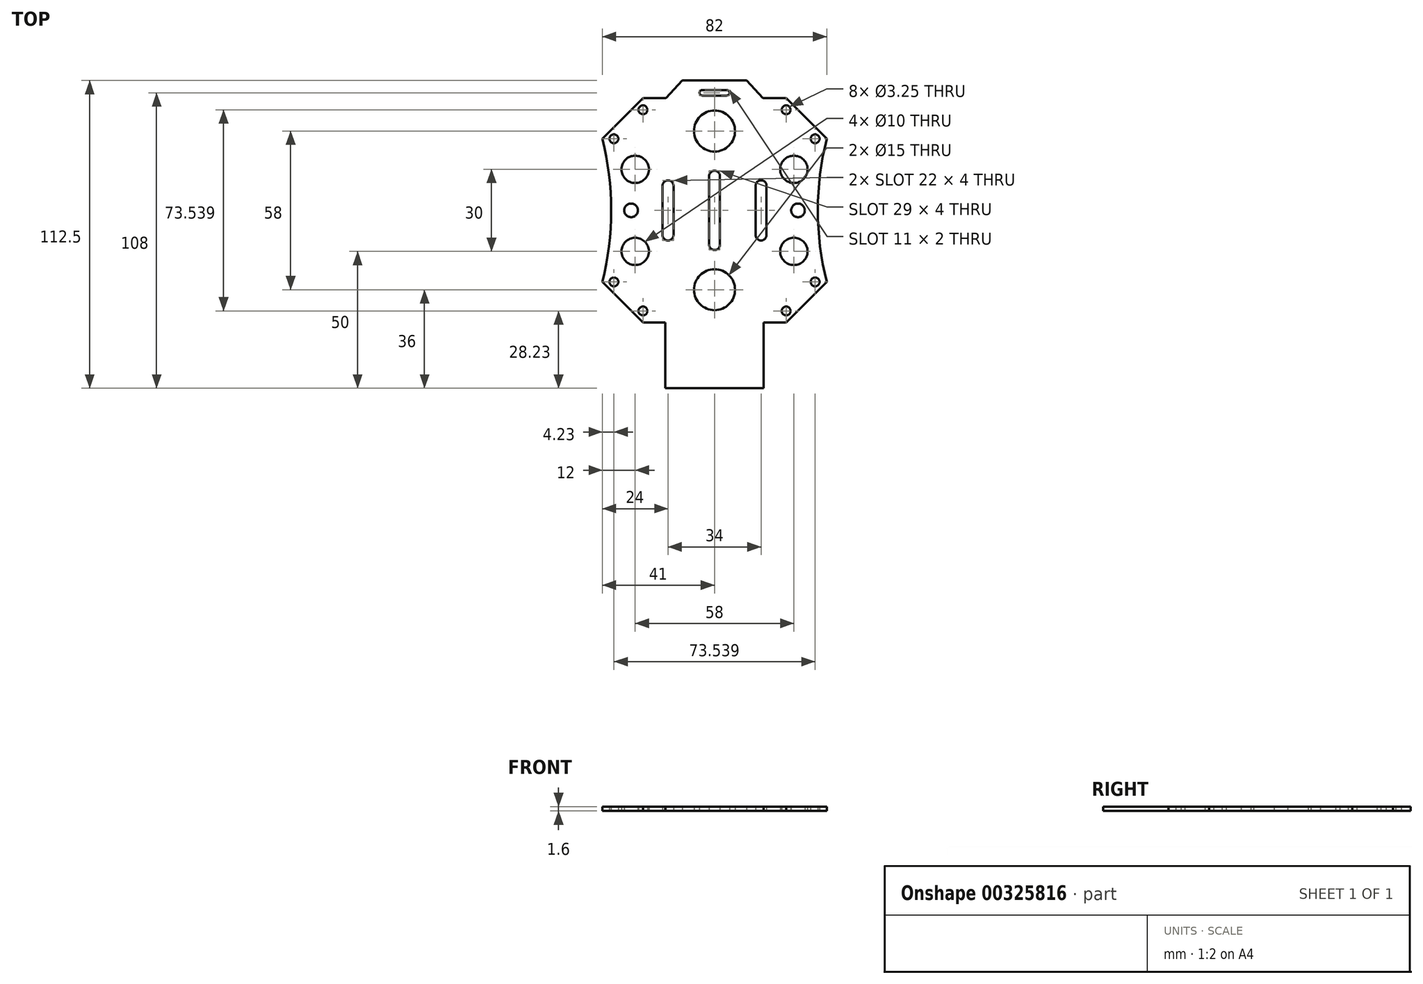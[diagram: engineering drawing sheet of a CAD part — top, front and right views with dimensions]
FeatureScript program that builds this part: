
annotation { "Feature Type Name" : "Feature", "Feature Type Description" : "" }
export const myFeature = defineFeature(function(context is Context, id is Id, definition is map)
    precondition{}
    {
        {
            var Q0;
            Q0=qCreatedBy(makeId("Top.planeOp"),FACE);
            var sketch = newSketch(context, id + "F0", { "sketchPlane" : qUnion([Q0])});
            skLineSegment(sketch, "E0.left", {"start": v(-2, 12.5) * mm, "end": v(-2, -12.5) * mm});
            skLineSegment(sketch, "E0.right", {"start": v(2, 12.5) * mm, "end": v(2, -12.5) * mm});
            skLineSegment(sketch, "E1", {"start": v(0, 0) * mm, "end": v(0, 54.3) * mm, "construction": true});
            skArc(sketch, "E2", {"start": v(2, 12.5) * mm, "mid": v(0, 14.5) * mm, "end": v(-2, 12.5) * mm});
            skArc(sketch, "E3", {"start": v(-2, -12.5) * mm, "mid": v(0, -14.5) * mm, "end": v(2, -12.5) * mm});
            skLineSegment(sketch, "E4", {"start": v(-64.66, 0) * mm, "end": v(96.62, 0) * mm, "construction": true});
            skLineSegment(sketch, "E5.left", {"start": v(-19, 9) * mm, "end": v(-19, -9) * mm});
            skLineSegment(sketch, "E5.right", {"start": v(-15, 9) * mm, "end": v(-15, -9) * mm});
            skArc(sketch, "E6", {"start": v(-15, 9) * mm, "mid": v(-17, 11) * mm, "end": v(-19, 9) * mm});
            skArc(sketch, "E7", {"start": v(-19, -9) * mm, "mid": v(-17, -11) * mm, "end": v(-15, -9) * mm});
            skArc(sketch, "E8.MirrorCS", {"start": v(19, -9) * mm, "mid": v(17, -11) * mm, "end": v(15, -9) * mm});
            skArc(sketch, "E9.MirrorCS", {"start": v(15, 9) * mm, "mid": v(17, 11) * mm, "end": v(19, 9) * mm});
            skLineSegment(sketch, "E10.MirrorCS", {"start": v(15, 9) * mm, "end": v(15, -9) * mm});
            skLineSegment(sketch, "E11.MirrorCS", {"start": v(19, 9) * mm, "end": v(19, -9) * mm});
            skCircle(sketch, "E12", {"center": v(-30.5, 0) * mm, "radius": 2.5 * mm});
            skCircle(sketch, "E13.MirrorC", {"center": v(30.5, 0) * mm, "radius": 2.5 * mm});
            skCircle(sketch, "E14", {"center": v(0, 29) * mm, "radius": 7.5 * mm});
            skCircle(sketch, "E15.MirrorC", {"center": v(0, -29) * mm, "radius": 7.5 * mm});
            skCircle(sketch, "E16", {"center": v(-29, 15) * mm, "radius": 5 * mm});
            skCircle(sketch, "E17.MirrorC", {"center": v(29, 15) * mm, "radius": 5 * mm});
            skCircle(sketch, "E18.MirrorC", {"center": v(-29, -15) * mm, "radius": 5 * mm});
            skCircle(sketch, "E19.MirrorC", {"center": v(29, -15) * mm, "radius": 5 * mm});
            skLineSegment(sketch, "E20.bottom", {"start": v(-4.5, 44) * mm, "end": v(4.5, 44) * mm});
            skLineSegment(sketch, "E20.top", {"start": v(-4.5, 42) * mm, "end": v(4.5, 42) * mm});
            skLineSegment(sketch, "E20.left", {"start": v(-4.5, 44) * mm, "end": v(-4.5, 42) * mm, "construction": true});
            skLineSegment(sketch, "E20.right", {"start": v(4.5, 44) * mm, "end": v(4.5, 42) * mm, "construction": true});
            skArc(sketch, "E21", {"start": v(-4.5, 44) * mm, "mid": v(-5.5, 43) * mm, "end": v(-4.5, 42) * mm});
            skArc(sketch, "E22", {"start": v(4.5, 42) * mm, "mid": v(5.5, 43) * mm, "end": v(4.5, 44) * mm});
            skLineSegment(sketch, "E23", {"start": v(-11.75, 47.5) * mm, "end": v(11.75, 47.5) * mm});
            skLineSegment(sketch, "E24", {"start": v(-18, -65) * mm, "end": v(18, -65) * mm});
            skArc(sketch, "E25", {"start": v(-41, -26.18) * mm, "mid": v(-37.75, 0) * mm, "end": v(-41, 26.18) * mm});
            skLineSegment(sketch, "E26", {"start": v(-41, 26.18) * mm, "end": v(-26.18, 41) * mm});
            skLineSegment(sketch, "E27", {"start": v(-26.18, 41) * mm, "end": v(-17.75, 41) * mm});
            skLineSegment(sketch, "E28", {"start": v(-17.75, 41) * mm, "end": v(-11.75, 47.5) * mm});
            skLineSegment(sketch, "E29", {"start": v(0, 0) * mm, "end": v(-64.55, 64.55) * mm, "construction": true});
            skLineSegment(sketch, "E30.MirrorCS", {"start": v(-41, -26.18) * mm, "end": v(-26.18, -41) * mm});
            skLineSegment(sketch, "E31", {"start": v(-18, -65) * mm, "end": v(-18, -41) * mm});
            skLineSegment(sketch, "E32", {"start": v(-18, -41) * mm, "end": v(-26.18, -41) * mm});
            skLineSegment(sketch, "E33.MirrorCS", {"start": v(41, 26.18) * mm, "end": v(26.18, 41) * mm});
            skLineSegment(sketch, "E34.MirrorCS", {"start": v(26.18, 41) * mm, "end": v(17.75, 41) * mm});
            skLineSegment(sketch, "E35.MirrorCS", {"start": v(17.75, 41) * mm, "end": v(11.75, 47.5) * mm});
            skArc(sketch, "E36.MirrorCS", {"start": v(41, -26.18) * mm, "mid": v(37.75, 0) * mm, "end": v(41, 26.18) * mm});
            skLineSegment(sketch, "E37.MirrorCS", {"start": v(41, -26.18) * mm, "end": v(26.18, -41) * mm});
            skLineSegment(sketch, "E38.MirrorCS", {"start": v(18, -41) * mm, "end": v(26.18, -41) * mm});
            skLineSegment(sketch, "E39.MirrorCS", {"start": v(18, -65) * mm, "end": v(18, -41) * mm});
            skCircle(sketch, "E40", {"center": v(-26.16, 36.77) * mm, "radius": 1.63 * mm});
            skCircle(sketch, "E41", {"center": v(-36.77, 26.16) * mm, "radius": 1.63 * mm});
            skLineSegment(sketch, "E42", {"start": v(-21.93, 41) * mm, "end": v(-40.2, 22.74) * mm, "construction": true});
            skCircle(sketch, "E43.1.0", {"center": v(-36.77, -26.16) * mm, "radius": 1.63 * mm});
            skCircle(sketch, "E43.1.1", {"center": v(-26.16, -36.77) * mm, "radius": 1.63 * mm});
            skCircle(sketch, "E43.2.0", {"center": v(26.16, -36.77) * mm, "radius": 1.63 * mm});
            skCircle(sketch, "E43.2.1", {"center": v(36.77, -26.16) * mm, "radius": 1.63 * mm});
            skCircle(sketch, "E43.3.0", {"center": v(36.77, 26.16) * mm, "radius": 1.63 * mm});
            skCircle(sketch, "E43.3.1", {"center": v(26.16, 36.77) * mm, "radius": 1.63 * mm});
            skPoint(sketch, "E43.center", {"position": v(0, 0) * mm});
            skSolve(sketch);
        }
        {
            var Q0;
            Q0=makeQuery(id+"F0.imprint","IMPRINT",FACE,{"disambiguationData":[TD([[makeQuery(id+"F0.imprint","IMPRINT",EDGE,{"derivedFrom":sQuery(id+"F0.wireOp",EDGE,"E0.left")}),-1.0]])]});
            extrude(context, id + "F1", {"entities" : qUnion([Q0]), "depth" : 1.6 * mm});
        }
    });
